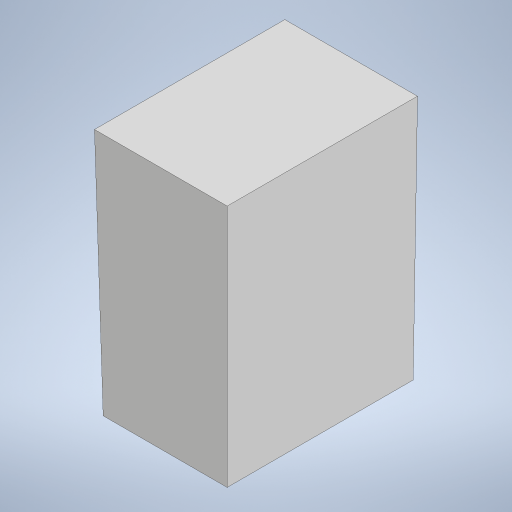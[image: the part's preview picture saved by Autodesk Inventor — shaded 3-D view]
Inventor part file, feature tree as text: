
AUTODESK INVENTOR PART (.ipt)
format: ipt  version: 2023 (Build 270158000, 158)  size: 208,896 bytes
history: native  units: in
note: dims shown in document units (in); Inventor stores cm internally (conversion verified against a paired STEP export)
features: sketch x1, extrude x1, draft x1
ambient origin geometry x8: Origin, YZ Plane, XZ Plane, XY Plane, X Axis, Y Axis, Z Axis, Center Point
bodies: Solid1 (feature_tree)
feature tree (3):
  sketch  "Sketch1"  dims[d0=0.5in d1=1.0in d2=1.5in d3=0.5in d4=0.5in d5=2.0in d6=0.0in d20=0.0069in]
  extrude  "Extrusion1"  Depth=2.0in
  draft  "FaceDraft1"
